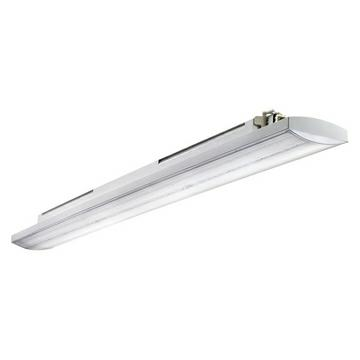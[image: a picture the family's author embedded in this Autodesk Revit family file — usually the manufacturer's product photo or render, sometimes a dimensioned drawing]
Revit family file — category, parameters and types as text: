
# Revit family: Lighting-Industrial-GEWISS-SMART[3]-WATERTIGHT-LED_TRASPARENT_1200mm
name_source: partatom
category: Apparecchi per illuminazione
units: mm (PartAtom-declared; Revit-internal decimal feet)

## family parameters
Condiviso = No
Host = Superficie
Punto di calcolo locali = Sì
Quota connettore circolare = Usa diametro
Sorgente d'illuminazione = No
Taglio con vuoti quando caricato = No
Tipo di parte = Normale

## types (1)
- Lighting-Industrial-GEWISS-SMART[3]-WATERTIGHT-LED_TRASPARENT_1200mm
    Application = Internal
    Catalogue = LIGHTING
    Catalogue Range = SMART [3]
    Colour temperature = 4000 K (CRI 80)
    Colour temperature: = 4000 K (CRI 80)
    Descrizione = SMART3 1200 63LED TRASP LP
    Device with reduced surface temperature = Complying
    Driver type = Constant Current Driver Led
    EAN code = 8011564876064
    Efficiency class of integrated LEDs = A ÷ A++
    Electrocod = 2434
    Failure rate apparecchio (35.000h, Tq=35° C) = <2,5%
    Failure rate apparecchio (50.000h, Tq=25° C) = <2,5%
    Ganci = GEWISS  - ALLUMINIO
    Glow Wire Test = 850°C
    IDF = 77bbed79-27d6-4dad-8951-2ae6e719d81a
    IDT = e9f9df53-c11c-4f09-88fd-a725bd6bd6c1
    IP degree = IP66/IP69
    Immagine tipo = GWS3136T.jpg
    Insulation class = II
    LED Life Time (L90B50) = 50000H
    LED Life time (L70) = 80000H
    LED Life time (L80B50) = 100000H
    LED LifeTime (L80B20) = 85000H
    Lamp = LED
    Lampada = LED
    Length = 1200 mm
    Lumen output (lm) = 4900
    Lunghezza Lampada = 1200 mm
    Modello = GWS3236TL
    No. LED (#) = 63
    Nominal flux (lm) = 5500
    Operating temperature: = -30 +50 °C
    Produttore = GEWISS S.p.A.
    Prospetto di default = 1219 mm
    SEO = Luminaire
    Schermo = Gewiss - Led Acceso
    Shield type = Transparent
    Shock resistance = IK08
    Stampa 1_100 = Sì
    Stampa 1_200 = No
    Struttura = GEWISS - SMART 3 - GRIGIO
    System power = 40W
    Technical sheet = https://www.gewiss.com
    Type of light source = LED - Not replaceable
    Typology = Stand alone
    URL = https://www.gewiss.com
    Version file RFA = 20.11
    Voltage = 220/240 V - 50/60 Hz - Stand alone
    Warranty = 5 years
    Weight (kg): = 2
    Working temperature = -25 +50 °C
